# Revit family: Vitra-Plural-64059
name_source: partatom
category: Furniture Systems
revit_build: Autodesk Revit 2017 (Build: 20160225_1515(x64)
units: mm (PartAtom-declared; Revit-internal decimal feet)

## family parameters
Cut with Voids When Loaded = No
Host = Face
OmniClass Number = 23.40.00.00
OmniClass Title = Equipment and Furnishings
Part Type = Normal
Room Calculation Point = No
Round Connector Dimension = Use Diameter
Shared = Yes

## types (1)
- Mirror-Vitra-Plural_64059
    Article No. (default) = 64059
    BIMobject category = Mirrors
    Construction Type = Face Mounted
    Default Elevation = 1200 mm
    Depth(mm) = 250 mm
    Description = Plural Mirror
    Design country = Turkey
    Height(mm) = 900 mm  [stored 2.95276 ft]
    IFC Classification = Furniture
    Manufacturer = Vitra
    Manufacturer name = Vitra
    Masterformat 2014 Code = 08 83 00
    Masterformat 2014 Description = Mirrors
    Model = 64059
    Nominal height = 0.000
    Nominal width = 0.000
    OmniClass Code = 23-21 00 00
    OmniClass Description = Furnishings, Fixtures and Equipment Products
    Primary Material = Vitra-DarkOlive
    Product SKU = 64059
    Product certification = https://vitraglobal.com
    Product data url = https://www.vitra.com.tr
    Product family = Plural
    Product group = Mirror
    Secondary Material = Vitra-DarkOlive
    Technical description = https://www.vitra.com.tr
    Thrid Material = Vitra-AmericanValnut
    UNSPSC Code = 56
    UNSPSC Description = Mirrors
    URL = https://vitraglobal.com
    Uniclass 1.4 Code = L8732
    Uniclass 1.4 Description = Mirrors
    Uniclass 2.0 Code = PR-71-55
    Uniclass 2.0 Description = Mirrors
    Uniclass 2015 Code = Pr_25_71_53
    Uniclass 2015 Name = Mirrors
    Uniformat II Code = E20
    Uniformat II Description = FURNISHINGS
    Warranty Period (Year) = 2
    Weight Net (kg) = 10,500
    Width(mm) = 380 mm
    Youtube = https://www.youtube.com

note: [stored X ft] marks values corroborated as IEEE doubles in the binary element streams (Revit-internal decimal feet)

## geometry (parser evidence)
native form markers: Sweep x3
no freeform markers — native parametric forms only
